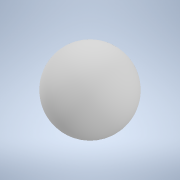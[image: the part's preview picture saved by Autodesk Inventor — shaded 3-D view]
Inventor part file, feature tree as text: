
AUTODESK INVENTOR PART (.ipt)
format: ipt  version: 2021 (Build 250183000, 183)  size: 117,760 bytes
history: native  units: mm
features: revolve x1, sketch x1
ambient origin geometry x8: Origin, YZ Plane, XZ Plane, XY Plane, X Axis, Y Axis, Z Axis, Center Point
bodies: Solid1 (feature_tree)
feature tree (2):
  revolve  "Revolution1"  Angle=90.0deg
  sketch  "Sketch2"  dims[d1=9.5mm d2=90.0deg]
